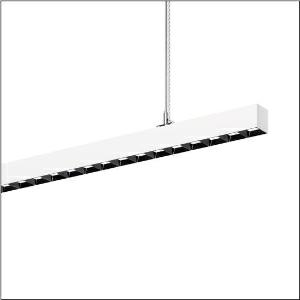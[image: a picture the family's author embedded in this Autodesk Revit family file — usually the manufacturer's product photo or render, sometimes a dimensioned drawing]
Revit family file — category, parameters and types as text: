
# Revit family: silica_21_51mx32tctdw
name_source: partatom
category: Lighting Fixtures
units: mm (PartAtom-declared; Revit-internal decimal feet)

## family parameters
Cut with Voids When Loaded = No
Host = Face
Light Source = No
Part Type = Normal
Room Calculation Point = No
Round Connector Dimension = Use Diameter
Shared = No

## types (1)
- --- (1 x LED, 15540 lm, 133.6 W, 6500K)
    Apparent Load = 134 VA
    CIE Flux Codes = 84 99 100 60 100
    Color Rendering = 80
    Color Temperature = 6500K
    Default Elevation = 1800 mm
    Description = Silica 21, office luminaire, primary light control with darklight reflector, of PMMA, black, CAT 2 (L<= 3000cd/m²), light emission: direct/indirect distribution, primary light characteristic: symmetric, installation type: suspended mounting, LED, rated luminous flux: 15.540lm, luminous efficacy: 111lm/W, light colour: 8tw, colour temperature: 2700..6500K, control gear: DALI DT8, with terminal, 3+2-pole, max. 2.5mm², mains connection: 220..240V, AC, 50/60Hz, rated input power: 140.3W, luminaire housing, of aluminium, traffic white (RAL 9016), length: 3.004mm, width: 53mm, height: 53mm, protection rating (complete): IP20, insulation class (complete): insulation class I (protective earthing), certification: CE, permissible operating ambient temperature: 0..+35°C, standard: EN 50419, packaging unit: 1 piece
    Height = 53 mm
    Lamp = 1 x LED
    Lamp Light Flux = 15540 lm
    Lamp Power = 133.6 W
    Lamp count = 1
    Length = 3004 mm
    Luminous efficacy = 116 lm/W
    Manufacturer = Siteco
    ModVariant = No
    Model = 51MX32TCTDW
    Mounting Place = Ceiling
    Mounting Type = Pendant
    Number of Poles = 1
    OnlyDefault = Yes
    Power Factor = 1
    Product Name = Silica 21
    Product group = office luminaire | ceiling pendant
    ProductGroupID = 903
    Protection Class = Protection class I
    Protection Degree = IP 20
    RLX_Detail_Level = 1
    RLX_Emergency_Light_Flux = 0 lm
    RLX_Emergency_Type = 0
    RLX_Emergency_Type_DB = No
    RlxData = <blob elided: 61321 chars, md5=1797e79b>
    Socket = socket
    Standby Power = 0 W
    System Light Flux = 15540 lm
    System Power = 134 W
    Type Comments = individual setting
    Type Image = l_1335871.jpg
    URL = http://relux.com
    VarID = @adj_141001
    Voltage = 0 V
    Weight = 0.00 kg
    Width = 53 mm

## geometry (parser evidence)
native form markers: Blend x4, Sweep x11
no freeform markers — native parametric forms only
